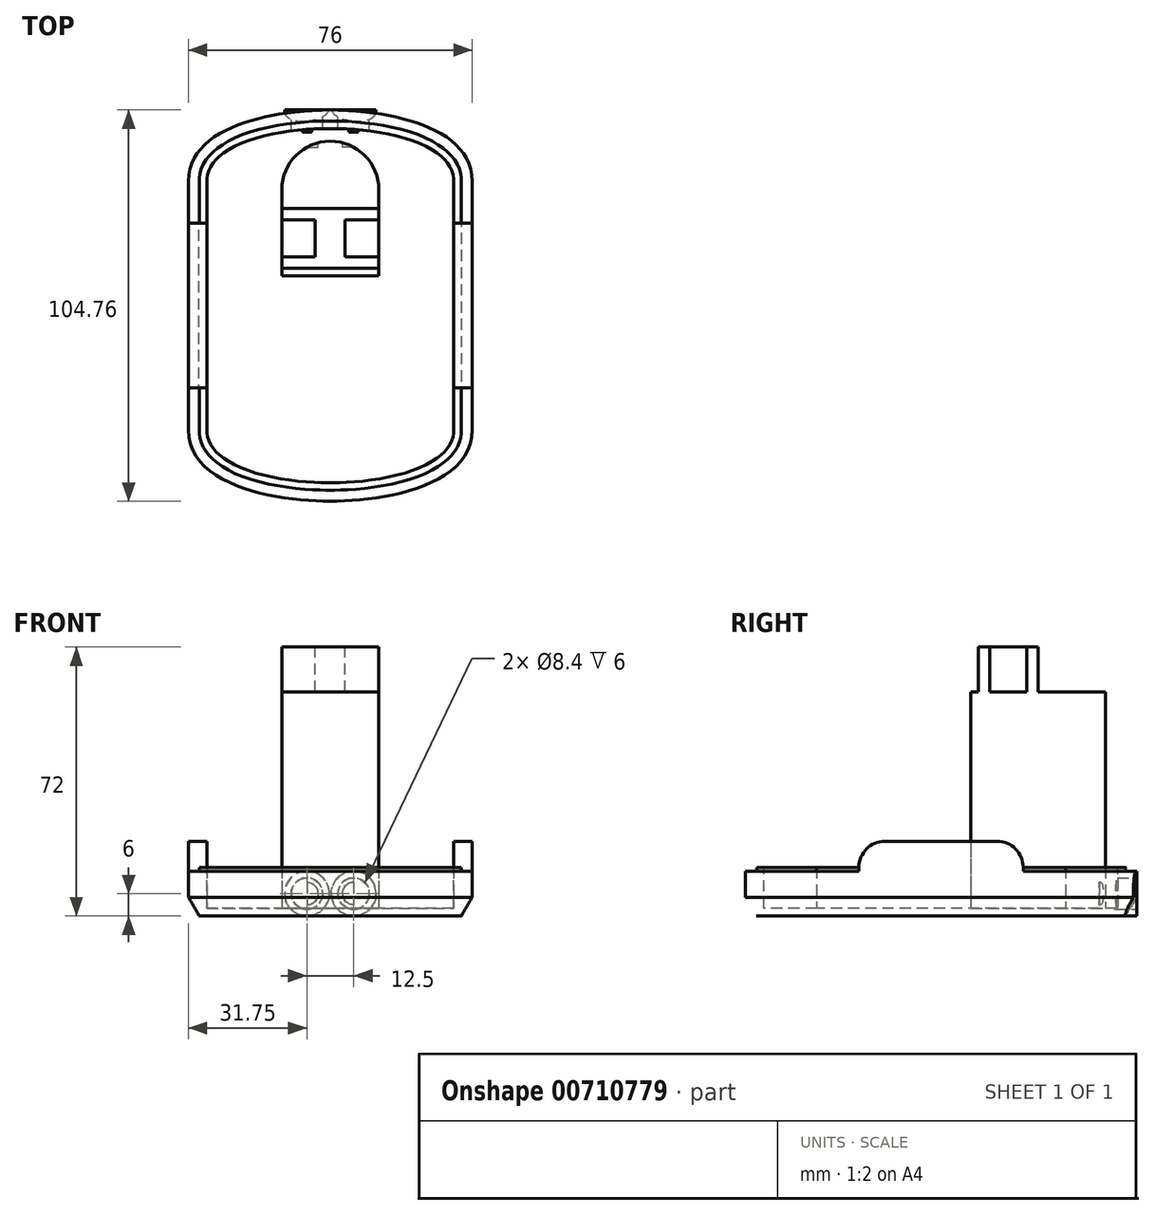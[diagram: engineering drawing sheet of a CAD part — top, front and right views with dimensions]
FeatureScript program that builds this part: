
annotation { "Feature Type Name" : "Feature", "Feature Type Description" : "" }
export const myFeature = defineFeature(function(context is Context, id is Id, definition is map)
    precondition{}
    {
        {
            var Q0;
            Q0=qCreatedBy(makeId("Top.planeOp"),FACE);
            var sketch = newSketch(context, id + "F0", { "sketchPlane" : qUnion([Q0])});
            skLineSegment(sketch, "E0", {"start": v(38, -59.88) * mm, "end": v(-38, 59.88) * mm, "construction": true});
            skPoint(sketch, "E1.startSnap0", {"position": v(0, 59.88) * mm});
            skFitSpline(sketch, "E2", {"points": [v(-38, 36.07) * mm, v(0, 55.15) * mm], "startDerivative": vector(0, 45.77) * mm, "endDerivative": vector(41.2, 0) * mm});
            skLineSegment(sketch, "E3", {"start": v(-38, 55.15) * mm, "end": v(38, 55.15) * mm, "construction": true});
            skLineSegment(sketch, "E4", {"start": v(-38, -30.53) * mm, "end": v(-38, 36.07) * mm});
            skLineSegment(sketch, "E5", {"start": v(-38, 2.77) * mm, "end": v(0, 2.77) * mm, "construction": true});
            skLineSegment(sketch, "E6", {"start": v(0, 2.77) * mm, "end": v(0, 55.15) * mm, "construction": true});
            skLineSegment(sketch, "E7.MirrorCS", {"start": v(0, 2.77) * mm, "end": v(0, -49.61) * mm, "construction": true});
            skFitSpline(sketch, "E8.MirrorCS", {"points": [v(-38, -30.53) * mm, v(0, -49.61) * mm], "startDerivative": vector(0, -45.77) * mm, "endDerivative": vector(41.2, 0) * mm});
            skFitSpline(sketch, "E9.MirrorCS", {"points": [v(38, 36.07) * mm, v(0, 55.15) * mm], "startDerivative": vector(0, 45.77) * mm, "endDerivative": vector(-41.2, 0) * mm});
            skFitSpline(sketch, "E10.MirrorCS", {"points": [v(38, -30.53) * mm, v(0, -49.61) * mm], "startDerivative": vector(0, -45.77) * mm, "endDerivative": vector(-41.2, 0) * mm});
            skLineSegment(sketch, "E11.MirrorCS", {"start": v(38, -30.53) * mm, "end": v(38, 36.07) * mm});
            skLineSegment(sketch, "E12", {"start": v(0, 2.77) * mm, "end": v(0, 0) * mm});
            skSolve(sketch);
        }
        {
            var Q0;
            Q0=qSketchRegion(id+"F0",true);
            extrude(context, id + "F1", {"entities" : qUnion([Q0]), "oppositeDirection" : true, "depth" : 12 * mm, "offsetDistance" : 25 * mm});
        }
        {
            var Q0;
            Q0=makeQuery(id+"F1.opExtrude","SWEPT_BODY",BODY,{"disambiguationData":[OSD([sQuery(id+"F0.wireOp",EDGE,"E2"),sQuery(id+"F0.wireOp",EDGE,"E4"),sQuery(id+"F0.wireOp",EDGE,"E8.MirrorCS"),sQuery(id+"F0.wireOp",EDGE,"E9.MirrorCS"),sQuery(id+"F0.wireOp",EDGE,"E10.MirrorCS"),sQuery(id+"F0.wireOp",EDGE,"E11.MirrorCS")])]});
            var Q1;
            Q1=sQuery(id+"F0.wireOp",EDGE,"E12");
            transform(context, id + "F2", {"entities" : qUnion([Q0]), "transformType" : TransformType.TRANSLATION_ENTITY, "oppositeDirectionEntity" : false, "transformLine" : qUnion([Q1]), "makeCopy" : false});
        }
        {
            var Q0;
            Q0=makeQuery(id+"F1.opExtrude","CAP_FACE",FACE,{"disambiguationData":[OSD([sQuery(id+"F0.wireOp",EDGE,"E2"),sQuery(id+"F0.wireOp",EDGE,"E4"),sQuery(id+"F0.wireOp",EDGE,"E8.MirrorCS"),sQuery(id+"F0.wireOp",EDGE,"E9.MirrorCS"),sQuery(id+"F0.wireOp",EDGE,"E10.MirrorCS"),sQuery(id+"F0.wireOp",EDGE,"E11.MirrorCS")])],"isStart":true});
            var sketch = newSketch(context, id + "F3", { "sketchPlane" : qUnion([Q0])});
            skFitSpline(sketch, "E13.0", {"points": [v(-35, -33.3) * mm, v(-35, -34.05) * mm, v(-34.85, -35.45) * mm, v(-34.25, -37.31) * mm, v(-33.28, -39.02) * mm, v(-31.93, -40.62) * mm, v(-30.2, -42.1) * mm, v(-27.45, -43.93) * mm, v(-23.24, -45.85) * mm, v(-17.42, -47.54) * mm, v(-11.29, -48.66) * mm, v(-5.28, -49.27) * mm, v(-1.65, -49.38) * mm, v(0, -49.38) * mm]});
            skLineSegment(sketch, "E13.1", {"start": v(35, -33.3) * mm, "end": v(35, 33.3) * mm});
            skFitSpline(sketch, "E13.2", {"points": [v(35, 33.3) * mm, v(35, 34.05) * mm, v(34.85, 35.45) * mm, v(34.25, 37.31) * mm, v(33.28, 39.02) * mm, v(31.93, 40.62) * mm, v(30.2, 42.1) * mm, v(27.45, 43.93) * mm, v(23.24, 45.85) * mm, v(17.42, 47.54) * mm, v(11.29, 48.66) * mm, v(5.28, 49.27) * mm, v(1.65, 49.38) * mm, v(0, 49.38) * mm]});
            skFitSpline(sketch, "E13.3", {"points": [v(0, -49.38) * mm, v(1.65, -49.38) * mm, v(5.28, -49.27) * mm, v(11.29, -48.66) * mm, v(17.42, -47.54) * mm, v(23.24, -45.85) * mm, v(27.45, -43.93) * mm, v(30.2, -42.1) * mm, v(31.93, -40.62) * mm, v(33.28, -39.02) * mm, v(34.25, -37.31) * mm, v(34.85, -35.45) * mm, v(35, -34.05) * mm, v(35, -33.3) * mm]});
            skFitSpline(sketch, "E13.4", {"points": [v(0, 49.38) * mm, v(-1.65, 49.38) * mm, v(-5.28, 49.27) * mm, v(-11.29, 48.66) * mm, v(-17.42, 47.54) * mm, v(-23.24, 45.85) * mm, v(-27.45, 43.93) * mm, v(-30.2, 42.1) * mm, v(-31.93, 40.62) * mm, v(-33.28, 39.02) * mm, v(-34.25, 37.31) * mm, v(-34.85, 35.45) * mm, v(-35, 34.05) * mm, v(-35, 33.3) * mm]});
            skLineSegment(sketch, "E13.5", {"start": v(-35, 33.3) * mm, "end": v(-35, -33.3) * mm});
            skFitSpline(sketch, "E14.0", {"points": [v(-33, -33.3) * mm, v(-33, -33.92) * mm, v(-32.88, -35.04) * mm, v(-32.4, -36.5) * mm, v(-31.63, -37.86) * mm, v(-30.51, -39.2) * mm, v(-29, -40.5) * mm, v(-26.51, -42.15) * mm, v(-22.57, -43.96) * mm, v(-16.97, -45.6) * mm, v(-11.01, -46.68) * mm, v(-5.14, -47.27) * mm, v(-1.6, -47.38) * mm, v(0, -47.38) * mm]});
            skLineSegment(sketch, "E14.1", {"start": v(33, -33.3) * mm, "end": v(33, 33.3) * mm});
            skFitSpline(sketch, "E14.2", {"points": [v(33, 33.3) * mm, v(33, 33.92) * mm, v(32.88, 35.04) * mm, v(32.4, 36.5) * mm, v(31.63, 37.86) * mm, v(30.51, 39.2) * mm, v(29, 40.5) * mm, v(26.51, 42.15) * mm, v(22.57, 43.96) * mm, v(16.97, 45.6) * mm, v(11.01, 46.68) * mm, v(5.14, 47.27) * mm, v(1.6, 47.38) * mm, v(0, 47.38) * mm]});
            skFitSpline(sketch, "E14.3", {"points": [v(0, -47.38) * mm, v(1.6, -47.38) * mm, v(5.14, -47.27) * mm, v(11.01, -46.68) * mm, v(16.97, -45.6) * mm, v(22.57, -43.96) * mm, v(26.51, -42.15) * mm, v(29, -40.5) * mm, v(30.51, -39.2) * mm, v(31.63, -37.86) * mm, v(32.4, -36.5) * mm, v(32.88, -35.04) * mm, v(33, -33.92) * mm, v(33, -33.3) * mm]});
            skFitSpline(sketch, "E14.4", {"points": [v(0, 47.38) * mm, v(-1.6, 47.38) * mm, v(-5.14, 47.27) * mm, v(-11.01, 46.68) * mm, v(-16.97, 45.6) * mm, v(-22.57, 43.96) * mm, v(-26.51, 42.15) * mm, v(-29, 40.5) * mm, v(-30.51, 39.2) * mm, v(-31.63, 37.86) * mm, v(-32.4, 36.5) * mm, v(-32.88, 35.04) * mm, v(-33, 33.92) * mm, v(-33, 33.3) * mm]});
            skLineSegment(sketch, "E14.5", {"start": v(-33, 33.3) * mm, "end": v(-33, -33.3) * mm});
            skLineSegment(sketch, "E15", {"start": v(-20.94, 44.38) * mm, "end": v(20.94, 44.38) * mm});
            skLineSegment(sketch, "E16.bottom", {"start": v(-13, 8) * mm, "end": v(13, 8) * mm});
            skLineSegment(sketch, "E16.left", {"start": v(-13, 8) * mm, "end": v(-13, 31) * mm});
            skLineSegment(sketch, "E16.right", {"start": v(13, 8) * mm, "end": v(13, 31) * mm});
            skArc(sketch, "E17", {"start": v(13, 31) * mm, "mid": v(0, 44) * mm, "end": v(-13, 31) * mm});
            skSolve(sketch);
        }
        {
            var Q0;
            Q0=qSketchRegion(id+"F3",true);
            var Q1;
            {var subQ3=sQuery(id+"F3.wireOp",EDGE,"E15");Q1=makeQuery(id+"F3.imprint","IMPRINT",FACE,{"disambiguationData":[TD([[makeQuery(id+"F3.imprint","IMPRINT",EDGE,{"derivedFrom":subQ3}),1.0]])]});}
            extrude(context, id + "F4", {"entities" : qUnion([Q0, Q1]), "operationType" : NewBodyOperationType.ADD, "depth" : 1 * mm, "offsetDistance" : 25 * mm});
        }
        {
            var Q0;
            Q0=makeQuery(id+"F3.imprint","IMPRINT",FACE,{"disambiguationData":[TD([[makeQuery(id+"F3.imprint","IMPRINT",EDGE,{"derivedFrom":sQuery(id+"F3.wireOp",EDGE,"E16.bottom")}),1.0]])]});
            extrude(context, id + "F5", {"entities" : qUnion([Q0]), "operationType" : NewBodyOperationType.ADD, "depth" : 60 * mm, "offsetDistance" : 25 * mm});
        }
        {
            var Q0;
            Q0=qCreatedBy(makeId("Right.planeOp"),FACE);
            var sketch = newSketch(context, id + "F6", { "sketchPlane" : qUnion([Q0])});
            skLineSegment(sketch, "E18.bottom", {"start": v(-22, 8) * mm, "end": v(22, 8) * mm});
            skLineSegment(sketch, "E18.top", {"start": v(-22, -8) * mm, "end": v(22, -8) * mm});
            skLineSegment(sketch, "E18.left", {"start": v(-22, 8) * mm, "end": v(-22, -8) * mm});
            skLineSegment(sketch, "E18.right", {"start": v(22, 8) * mm, "end": v(22, -8) * mm});
            skPoint(sketch, "E18.middle", {"position": v(0, 0) * mm});
            skSolve(sketch);
        }
        {
            var Q0;
            Q0=qSketchRegion(id+"F6",true);
            extrude(context, id + "F7", {"entities" : qUnion([Q0]), "operationType" : NewBodyOperationType.ADD, "depth" : 76 * mm, "offsetDistance" : 25 * mm, "symmetric" : true});
        }
        {
            var Q0;
            Q0=makeQuery(id+"F7.opExtrude","SWEPT_EDGE",EDGE,{"disambiguationData":[OSD([sQuery(id+"F6.wireOp",EDGE,"E18.bottom"),sQuery(id+"F6.wireOp",EDGE,"E18.right")])]});
            var Q1;
            Q1=makeQuery(id+"F7.opExtrude","SWEPT_EDGE",EDGE,{"disambiguationData":[OSD([sQuery(id+"F6.wireOp",EDGE,"E18.bottom"),sQuery(id+"F6.wireOp",EDGE,"E18.left")])]});
            fillet(context, id + "F8", {"entities" : qUnion([Q0, Q1]), "radius" : 7 * mm, "tangentPropagation" : true, "allowEdgeOverflow" : false});
        }
        {
            var Q0;
            Q0=makeQuery(id+"F3.imprint","IMPRINT",FACE,{"disambiguationData":[TD([[makeQuery(id+"F3.imprint","IMPRINT",EDGE,{"derivedFrom":sQuery(id+"F3.wireOp",EDGE,"E14.0")}),1.0]])]});
            extrude(context, id + "F9", {"entities" : qUnion([Q0]), "operationType" : NewBodyOperationType.REMOVE, "oppositeDirection" : true, "depth" : 10 * mm, "offsetDistance" : 25 * mm, "hasSecondDirection" : true, "secondDirectionBound" : BoundingType.THROUGH_ALL, "secondDirectionOppositeDirection" : false, "secondDirectionDepth" : 25 * mm});
        }
        {
            var Q0;
            Q0=makeQuery(id+"F1.opExtrude","CAP_EDGE",EDGE,{"disambiguationData":[OSD([sQuery(id+"F0.wireOp",EDGE,"E10.MirrorCS")])],"isStart":false});
            var Q1;
            Q1=makeQuery(id+"F1.opExtrude","CAP_EDGE",EDGE,{"disambiguationData":[OSD([sQuery(id+"F0.wireOp",EDGE,"E8.MirrorCS")])],"isStart":false});
            chamfer(context, id + "F10", {"entities" : qUnion([Q0, Q1]), "chamferType" : ChamferType.OFFSET_ANGLE, "width" : 5 * mm, "oppositeDirection" : true, "angle" : 30 * degree, "tangentPropagation" : true});
        }
        {
            var Q0;
            Q0=qCreatedBy(makeId("Front.planeOp"),FACE);
            var Q1;
            Q1=makeQuery(id+"F1.opExtrude","CAP_VERTEX",VERTEX,{"disambiguationData":[OSD([sQuery(id+"F0.wireOp",EDGE,"E2"),sQuery(id+"F0.wireOp",EDGE,"E9.MirrorCS")])],"isStart":true});
            cPlane(context, id + "F11", {"entities" : qUnion([Q0, Q1]), "cplaneType" : CPlaneType.PLANE_POINT, "offset" : 25 * mm, "width" : 150 * mm, "height" : 150 * mm});
        }
        {
            var Q0;
            Q0=qCreatedBy(id+"F11.planeOp",FACE);
            var sketch = newSketch(context, id + "F12", { "sketchPlane" : qUnion([Q0])});
            skLineSegment(sketch, "E19", {"start": v(0, 0) * mm, "end": v(0, -6) * mm, "construction": true});
            skLineSegment(sketch, "E20", {"start": v(-6.25, -6) * mm, "end": v(6.25, -6) * mm, "construction": true});
            skCircle(sketch, "E21", {"center": v(-6.25, -6) * mm, "radius": 4.2 * mm});
            skCircle(sketch, "E22", {"center": v(6.25, -6) * mm, "radius": 4.2 * mm});
            skCircle(sketch, "E23", {"center": v(6.25, -6) * mm, "radius": 6 * mm});
            skCircle(sketch, "E24", {"center": v(-6.25, -6) * mm, "radius": 6 * mm});
            skCircle(sketch, "E25", {"center": v(-6.25, -6) * mm, "radius": 3 * mm});
            skCircle(sketch, "E26", {"center": v(6.25, -6) * mm, "radius": 3 * mm});
            skSolve(sketch);
        }
        {
            var Q0;
            Q0=qSketchRegion(id+"F12",true);
            var Q1;
            Q1=makeQuery(id+"F1.opExtrude","SWEPT_BODY",BODY,{"disambiguationData":[OSD([sQuery(id+"F0.wireOp",EDGE,"E2"),sQuery(id+"F0.wireOp",EDGE,"E4"),sQuery(id+"F0.wireOp",EDGE,"E8.MirrorCS"),sQuery(id+"F0.wireOp",EDGE,"E9.MirrorCS"),sQuery(id+"F0.wireOp",EDGE,"E10.MirrorCS"),sQuery(id+"F0.wireOp",EDGE,"E11.MirrorCS")])]});
            extrude(context, id + "F13", {"entities" : qUnion([Q0]), "operationType" : NewBodyOperationType.ADD, "endBound" : BoundingType.UP_TO_BODY, "depth" : 25 * mm, "endBoundEntityBody" : qUnion([Q1]), "offsetDistance" : 25 * mm});
        }
        {
            var Q0;
            Q0=makeQuery(id+"F12.imprint","IMPRINT",FACE,{"disambiguationData":[TD([[makeQuery(id+"F12.imprint","IMPRINT",EDGE,{"derivedFrom":sQuery(id+"F12.wireOp",EDGE,"E22")}),1.0]])]});
            var Q1;
            Q1=makeQuery(id+"F12.imprint","IMPRINT",FACE,{"disambiguationData":[TD([[makeQuery(id+"F12.imprint","IMPRINT",EDGE,{"derivedFrom":sQuery(id+"F12.wireOp",EDGE,"E21")}),1.0]])]});
            extrude(context, id + "F14", {"entities" : qUnion([Q0, Q1]), "operationType" : NewBodyOperationType.REMOVE, "depth" : 6 * mm, "offsetDistance" : 25 * mm});
        }
        {
            var Q0;
            Q0=makeQuery(id+"F12.imprint","IMPRINT",FACE,{"disambiguationData":[TD([[makeQuery(id+"F12.imprint","IMPRINT",EDGE,{"derivedFrom":sQuery(id+"F12.wireOp",EDGE,"E26")}),1.0]])]});
            var Q1;
            Q1=makeQuery(id+"F12.imprint","IMPRINT",FACE,{"disambiguationData":[TD([[makeQuery(id+"F12.imprint","IMPRINT",EDGE,{"derivedFrom":sQuery(id+"F12.wireOp",EDGE,"E25")}),1.0]])]});
            extrude(context, id + "F15", {"entities" : qUnion([Q0, Q1]), "operationType" : NewBodyOperationType.REMOVE, "depth" : 10 * mm, "offsetDistance" : 25 * mm});
        }
        {
            var Q0;
            Q0=makeQuery(id+"F5.opExtrude","CAP_FACE",FACE,{"disambiguationData":[OSD([sQuery(id+"F3.wireOp",EDGE,"E16.bottom"),sQuery(id+"F3.wireOp",EDGE,"E16.left"),sQuery(id+"F3.wireOp",EDGE,"E16.right"),sQuery(id+"F3.wireOp",EDGE,"E17")])],"isStart":false});
            var sketch = newSketch(context, id + "F16", { "sketchPlane" : qUnion([Q0])});
            skLineSegment(sketch, "E27", {"start": v(-13, 10) * mm, "end": v(13, 10) * mm});
            skLineSegment(sketch, "E28", {"start": v(-13, 26) * mm, "end": v(13, 26) * mm});
            skLineSegment(sketch, "E29.bottom", {"start": v(-13, 13) * mm, "end": v(-4, 13) * mm});
            skLineSegment(sketch, "E29.top", {"start": v(-13, 23) * mm, "end": v(-4, 23) * mm});
            skLineSegment(sketch, "E29.left", {"start": v(-13, 13) * mm, "end": v(-13, 23) * mm});
            skLineSegment(sketch, "E29.right", {"start": v(-4, 13) * mm, "end": v(-4, 23) * mm});
            skLineSegment(sketch, "E30", {"start": v(0, 0) * mm, "end": v(0, 44) * mm, "construction": true});
            skLineSegment(sketch, "E31.MirrorCS", {"start": v(13, 23) * mm, "end": v(4, 23) * mm});
            skLineSegment(sketch, "E32.MirrorCS", {"start": v(13, 13) * mm, "end": v(4, 13) * mm});
            skLineSegment(sketch, "E33.MirrorCS", {"start": v(13, 13) * mm, "end": v(13, 23) * mm});
            skLineSegment(sketch, "E34.MirrorCS", {"start": v(4, 13) * mm, "end": v(4, 23) * mm});
            skSolve(sketch);
        }
        {
            var Q0;
            Q0=makeQuery(id+"F16.imprint","IMPRINT",FACE,{"disambiguationData":[TD([[makeQuery(id+"F16.imprint","IMPRINT",EDGE,{"derivedFrom":sQuery(id+"F16.wireOp",EDGE,"E29.bottom")}),1.0]])]});
            var Q1;
            {var subQ0=sQuery(id+"F16.wireOp",EDGE,"E27");Q1=makeQuery(id+"F16.imprint","IMPRINT",FACE,{"disambiguationData":[TD([[makeQuery(id+"F16.imprint","IMPRINT",EDGE,{"derivedFrom":subQ0}),-1.0]])]});}
            var Q2;
            Q2=makeQuery(id+"F16.imprint","IMPRINT",FACE,{"disambiguationData":[TD([[makeQuery(id+"F16.imprint","IMPRINT",EDGE,{"derivedFrom":sQuery(id+"F16.wireOp",EDGE,"E31.MirrorCS")}),1.0]])]});
            var Q3;
            {var subQ0=sQuery(id+"F16.wireOp",EDGE,"E28");Q3=makeQuery(id+"F16.imprint","IMPRINT",FACE,{"disambiguationData":[TD([[makeQuery(id+"F16.imprint","IMPRINT",EDGE,{"derivedFrom":subQ0}),1.0]])]});}
            extrude(context, id + "F17", {"entities" : qUnion([Q0, Q1, Q2, Q3]), "operationType" : NewBodyOperationType.REMOVE, "oppositeDirection" : true, "depth" : 12 * mm, "offsetDistance" : 25 * mm});
        }
    });
